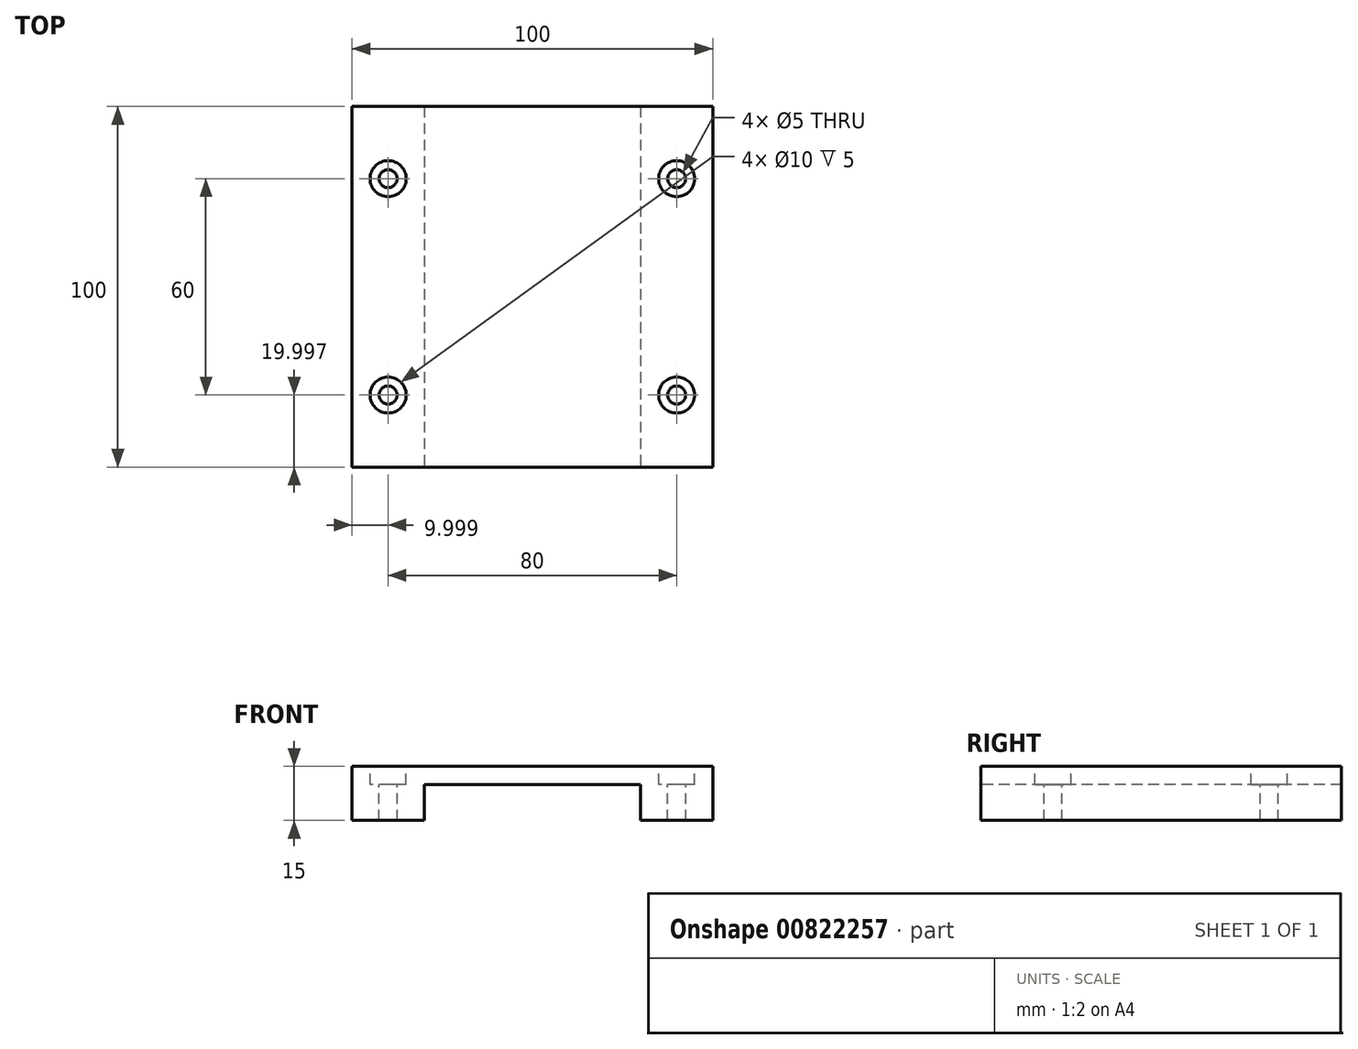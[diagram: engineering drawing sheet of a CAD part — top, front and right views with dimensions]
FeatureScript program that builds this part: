
annotation { "Feature Type Name" : "Feature", "Feature Type Description" : "" }
export const myFeature = defineFeature(function(context is Context, id is Id, definition is map)
    precondition{}
    {
        {
            var Q0;
            Q0=qCreatedBy(makeId("Top.planeOp"),FACE);
            var sketch = newSketch(context, id + "F0", { "sketchPlane" : qUnion([Q0])});
            skLineSegment(sketch, "E0.bottom", {"start": v(-73, 67.99) * mm, "end": v(-13, 67.99) * mm});
            skLineSegment(sketch, "E0.top", {"start": v(-73, -32.01) * mm, "end": v(-13, -32.01) * mm});
            skLineSegment(sketch, "E0.left", {"start": v(-73, 67.99) * mm, "end": v(-73, -32.01) * mm});
            skLineSegment(sketch, "E0.right", {"start": v(-13, 67.99) * mm, "end": v(-13, -32.01) * mm});
            skLineSegment(sketch, "E1", {"start": v(-43, 67.99) * mm, "end": v(-43, -32.01) * mm});
            skLineSegment(sketch, "E2.bottom", {"start": v(-73, 67.99) * mm, "end": v(-93, 67.99) * mm});
            skLineSegment(sketch, "E2.top", {"start": v(-73, -32.01) * mm, "end": v(-93, -32.01) * mm});
            skLineSegment(sketch, "E2.right", {"start": v(-93, 67.99) * mm, "end": v(-93, -32.01) * mm});
            skLineSegment(sketch, "E3.MirrorCS", {"start": v(7, 67.99) * mm, "end": v(7, -32.01) * mm});
            skLineSegment(sketch, "E4.MirrorCS", {"start": v(-13, 67.99) * mm, "end": v(7, 67.99) * mm});
            skLineSegment(sketch, "E5.MirrorCS", {"start": v(-13, -32.01) * mm, "end": v(7, -32.01) * mm});
            skSolve(sketch);
        }
        {
            var Q0;
            {var subQ2=sQuery(id+"F0.wireOp",EDGE,"E1");Q0=makeQuery(id+"F0.imprint","IMPRINT",FACE,{"disambiguationData":[TD([[makeQuery(id+"F0.imprint","IMPRINT",EDGE,{"derivedFrom":subQ2}),-1.0]])]});}
            var Q1;
            {var subQ0=sQuery(id+"F0.wireOp",EDGE,"E0.right");Q1=makeQuery(id+"F0.imprint","IMPRINT",FACE,{"disambiguationData":[TD([[makeQuery(id+"F0.imprint","IMPRINT",EDGE,{"derivedFrom":subQ0}),-1.0]])]});}
            extrude(context, id + "F1", {"entities" : qUnion([Q0, Q1]), "depth" : 5 * mm, "offsetDistance" : 25 * mm});
        }
        {
            var Q0;
            Q0=makeQuery(id+"F0.imprint","IMPRINT",FACE,{"disambiguationData":[TD([[makeQuery(id+"F0.imprint","IMPRINT",EDGE,{"derivedFrom":sQuery(id+"F0.wireOp",EDGE,"E2.bottom")}),1.0]])]});
            var Q1;
            Q1=makeQuery(id+"F0.imprint","IMPRINT",FACE,{"disambiguationData":[TD([[makeQuery(id+"F0.imprint","IMPRINT",EDGE,{"derivedFrom":sQuery(id+"F0.wireOp",EDGE,"E0.right")}),1.0]])]});
            extrude(context, id + "F2", {"entities" : qUnion([Q0, Q1]), "operationType" : NewBodyOperationType.ADD, "oppositeDirection" : true, "depth" : 10 * mm, "offsetDistance" : 25 * mm, "hasSecondDirection" : true, "secondDirectionOppositeDirection" : false, "secondDirectionDepth" : 5 * mm});
        }
        {
            var Q0;
            {var subQ0=sQuery(id+"F0.wireOp",EDGE,"E0.left");var subQ1=sQuery(id+"F0.wireOp",EDGE,"E0.right");Q0=makeQuery(id+"F2.boolean.opBoolean","MERGE",FACE,{"derivedFrom":[makeQuery(id+"F1.opExtrude","CAP_FACE",FACE,{"disambiguationData":[OSD([sQuery(id+"F0.wireOp",EDGE,"E0.bottom"),sQuery(id+"F0.wireOp",EDGE,"E0.top"),subQ1,subQ0])],"isStart":false}),makeQuery(id+"F2.opExtrude","CAP_FACE",FACE,{"disambiguationData":[OSD([subQ1,sQuery(id+"F0.wireOp",EDGE,"E3.MirrorCS"),sQuery(id+"F0.wireOp",EDGE,"E4.MirrorCS"),sQuery(id+"F0.wireOp",EDGE,"E5.MirrorCS")])],"isStart":true}),makeQuery(id+"F2.opExtrude","CAP_FACE",FACE,{"disambiguationData":[OSD([sQuery(id+"F0.wireOp",EDGE,"E2.bottom"),sQuery(id+"F0.wireOp",EDGE,"E2.top"),subQ0,sQuery(id+"F0.wireOp",EDGE,"E2.right")])],"isStart":true})]});}
            var sketch = newSketch(context, id + "F3", { "sketchPlane" : qUnion([Q0])});
            skPoint(sketch, "E6", {"position": v(-83, 47.99) * mm});
            skPoint(sketch, "E7", {"position": v(-83, -12.01) * mm});
            skLineSegment(sketch, "E8", {"start": v(-43, -32.01) * mm, "end": v(-43, 67.99) * mm});
            skPoint(sketch, "E9.MirrorP", {"position": v(-3, 47.99) * mm});
            skPoint(sketch, "E10.MirrorP", {"position": v(-3, -12.01) * mm});
            skSolve(sketch);
        }
        {
            var Q0;
            Q0=sQuery(id+"F3.wireOp",VERTEX,"E7");
            var Q1;
            Q1=sQuery(id+"F3.wireOp",VERTEX,"E6");
            var Q2;
            Q2=sQuery(id+"F3.wireOp",VERTEX,"E9.MirrorP");
            var Q3;
            Q3=sQuery(id+"F3.wireOp",VERTEX,"E10.MirrorP");
            var Q4;
            Q4=makeQuery(id+"F1.opExtrude","SWEPT_BODY",BODY,{"disambiguationData":[OSD([sQuery(id+"F0.wireOp",EDGE,"E0.bottom"),sQuery(id+"F0.wireOp",EDGE,"E0.top"),sQuery(id+"F0.wireOp",EDGE,"E0.right"),sQuery(id+"F0.wireOp",EDGE,"E0.left")])]});
            hole(context, id + "F4", {"style" : HoleStyle.C_BORE, "endStyle" : HoleEndStyle.BLIND, "holeDiameter" : 5 * mm, "cBoreDiameter" : 10 * mm, "cBoreDepth" : 5 * mm, "majorDiameter" : 5 * mm, "holeDepth" : 30 * mm, "isTappedThrough" : true, "tappedDepth" : 12 * mm, "tapClearance" : 3, "locations" : qUnion([Q0, Q1, Q2, Q3]), "scope" : qUnion([Q4])});
        }
    });
